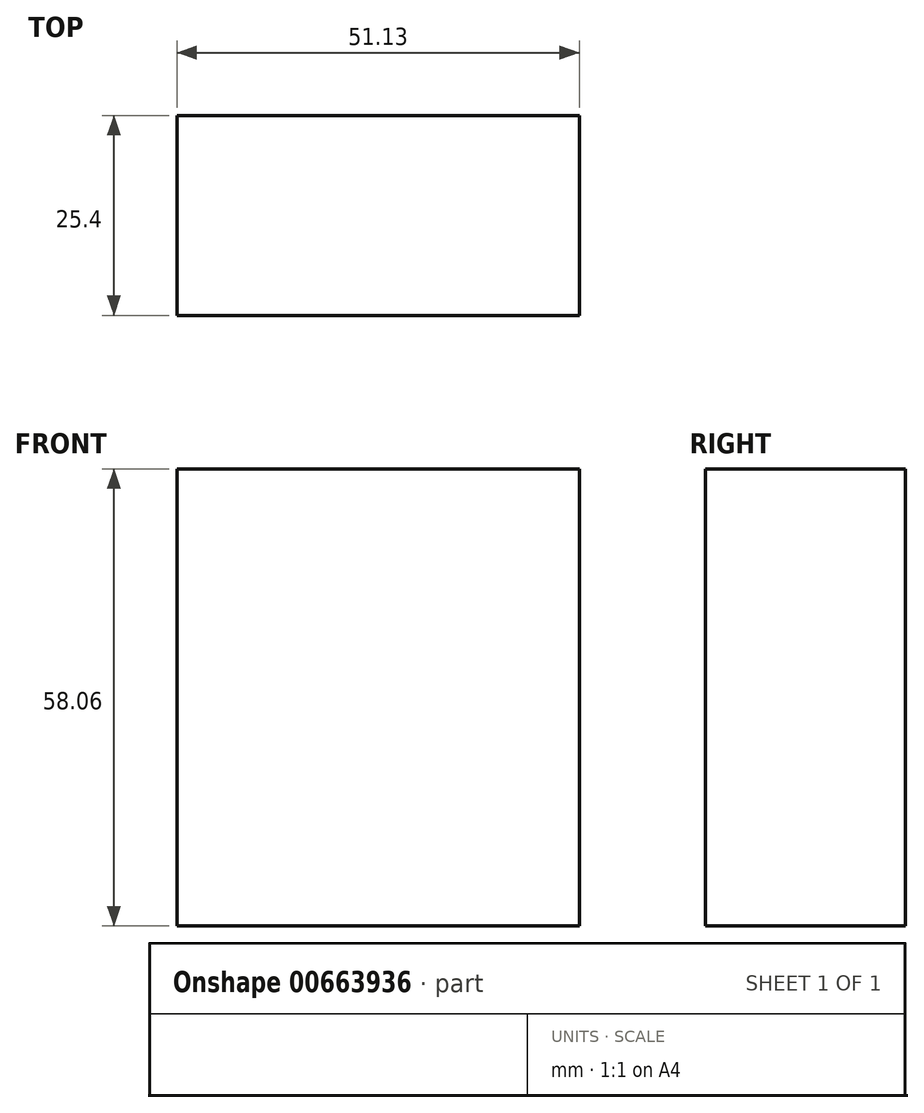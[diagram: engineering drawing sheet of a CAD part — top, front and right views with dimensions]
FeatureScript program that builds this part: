
annotation { "Feature Type Name" : "Feature", "Feature Type Description" : "" }
export const myFeature = defineFeature(function(context is Context, id is Id, definition is map)
    precondition{}
    {
        {
            var Q0;
            Q0=qCreatedBy(makeId("Front.planeOp"),FACE);
            var sketch = newSketch(context, id + "F0", { "sketchPlane" : qUnion([Q0])});
            skLineSegment(sketch, "E0.bottom", {"start": v(-23.31, 29.03) * mm, "end": v(27.82, 29.03) * mm});
            skLineSegment(sketch, "E0.top", {"start": v(-23.31, -29.03) * mm, "end": v(27.82, -29.03) * mm});
            skLineSegment(sketch, "E0.left", {"start": v(-23.31, 29.03) * mm, "end": v(-23.31, -29.03) * mm});
            skLineSegment(sketch, "E0.right", {"start": v(27.82, 29.03) * mm, "end": v(27.82, -29.03) * mm});
            skPoint(sketch, "E0.middle", {"position": v(2.26, 0) * mm});
            skSolve(sketch);
        }
        {
            var Q0;
            Q0=makeQuery(id+"F0.imprint","IMPRINT",FACE,{"disambiguationData":[TD([[makeQuery(id+"F0.imprint","IMPRINT",EDGE,{"derivedFrom":sQuery(id+"F0.wireOp",EDGE,"E0.bottom")}),-1.0]])]});
            extrude(context, id + "F1", {"entities" : qUnion([Q0]), "depth" : 25.4 * mm, "offsetDistance" : 25.4 * mm});
        }
    });
